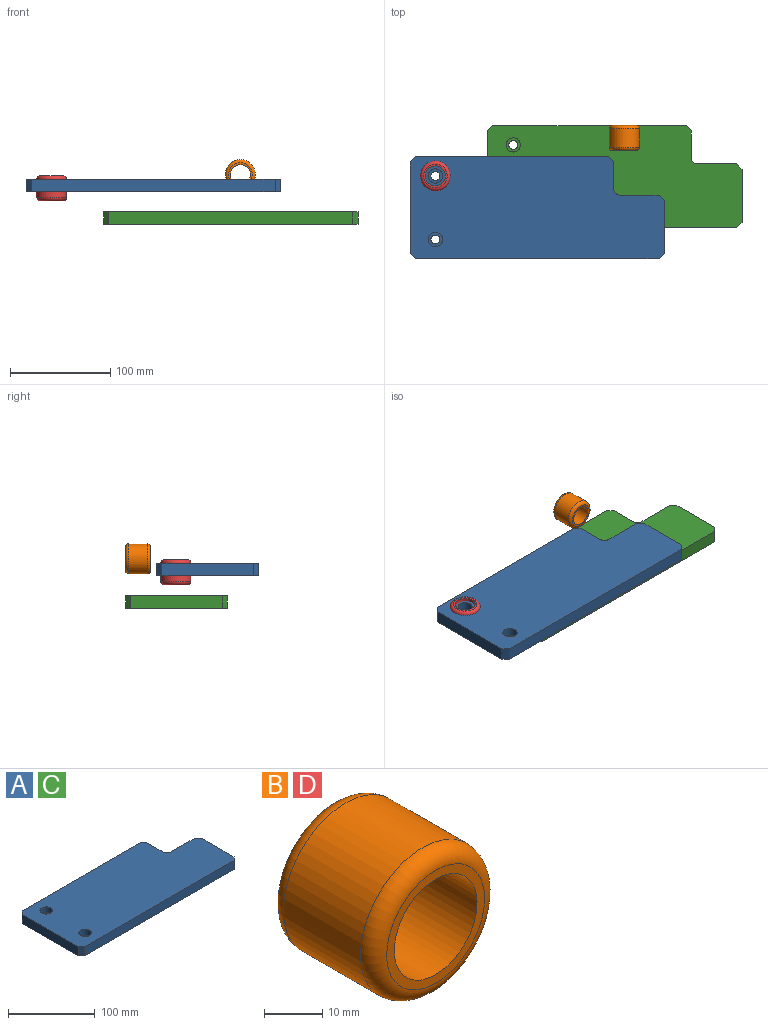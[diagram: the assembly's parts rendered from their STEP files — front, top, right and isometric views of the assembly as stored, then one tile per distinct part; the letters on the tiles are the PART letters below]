
ASSEMBLY  parts=4 mates=1
PART A: 20 faces, bbox 254x101.6x12.7 mm
  f0: plane 193.04x12.7mm, normal (0,1,0), area 2451.6mm2, adj f1,f2,f15,f18
  f1: plane 254x101.6mm, normal (0,0,1), area 23496.1mm2, adj f0,f3,f4,f5,f8,f11,f12,f13
  f2: plane 254x101.6mm, normal (0,0,-1), area 23687.8mm2, adj f0,f3,f4,f5,f6,f9,f12,f13
  f3: plane 243.84x12.7mm, normal (0,-1,0), area 3096.8mm2, adj f1,f2,f17,f19
  f4: plane 53.34x12.7mm, normal (1,0,0), area 677.4mm2, adj f1,f2,f16,f17
  f5: plane 91.44x12.7mm, normal (-1,0,0), area 1161.3mm2, adj f1,f2,f18,f19
  f6: cylinder r=4.5mm len=9mm, axis (0,0,1), area 132.9mm2, adj f2,f7
  f7: plane 14.25x14.25mm, normal (0,0,1), area 95.9mm2, adj f6,f8
  f8: cylinder r=7.12mm len=14.25mm, axis (0,0,1), area 358.1mm2, adj f1,f7
  f9: cylinder r=4.5mm len=9mm, axis (0,0,1), area 132.9mm2, adj f2,f10
  f10: plane 14.25x14.25mm, normal (0,0,1), area 95.9mm2, adj f9,f11
  f11: cylinder r=7.12mm len=14.25mm, axis (0,0,1), area 358.1mm2, adj f1,f10
  f12: plane 39.37x12.7mm, normal (0,1,0), area 500mm2, adj f1,f2,f14,f16
  f13: plane 26.67x12.7mm, normal (1,0,0), area 338.7mm2, adj f1,f2,f14,f15
  f14: cylinder r=6.35mm len=12.7mm, axis (0,0,1), area 126.7mm2, adj f1,f2,f12,f13
  f15: plane 12.7x5.08mm, normal (0.71,0.71,0), area 91.2mm2, adj f0,f1,f2,f13
  f16: plane 12.7x5.08mm, normal (0.71,0.71,0), area 91.2mm2, adj f1,f2,f4,f12
  f17: plane 12.7x5.08mm, normal (0.71,-0.71,0), area 91.2mm2, adj f1,f2,f3,f4
  f18: plane 12.7x5.08mm, normal (-0.71,0.71,0), area 91.2mm2, adj f0,f1,f2,f5
  f19: plane 12.7x5.08mm, normal (-0.71,-0.71,0), area 91.2mm2, adj f1,f2,f3,f5
PART B: 6 faces, bbox 32.5x25x32.5 mm
  f0: cylinder r=10mm len=25mm, axis (0,1,0), area 1570.8mm2, adj f2,f3
  f1: cylinder r=15mm len=30mm, axis (0,1,0), area 1757.7mm2, adj f4,f5
  f2: plane 23.65x23.65mm, normal (0,-1,0), area 125.1mm2, adj f0,f5
  f3: plane 23.65x23.65mm, normal (0,1,0), area 125.1mm2, adj f0,f4
  f4: torus R=11.83mm, axis (0,-1,0), area 433.9mm2, adj f1,f3
  f5: torus R=11.83mm, axis (0,-1,0), area 433.9mm2, adj f1,f2
PART C: same geometry as A
PART D: same geometry as B
PLACE A t=(-77.83,-31.1,32.64)mm
PLACE B t=(9.47,51.13,49.73)mm
PLACE C at identity
PLACE D rot(axis=(0.58,-0.58,-0.58),120deg) t=(-179.43,0.65,48.52)mm
MATE fastened D.f1 <-> A.f9  axis (0,0,1) through (-179.43,0.65,45.34)mm
